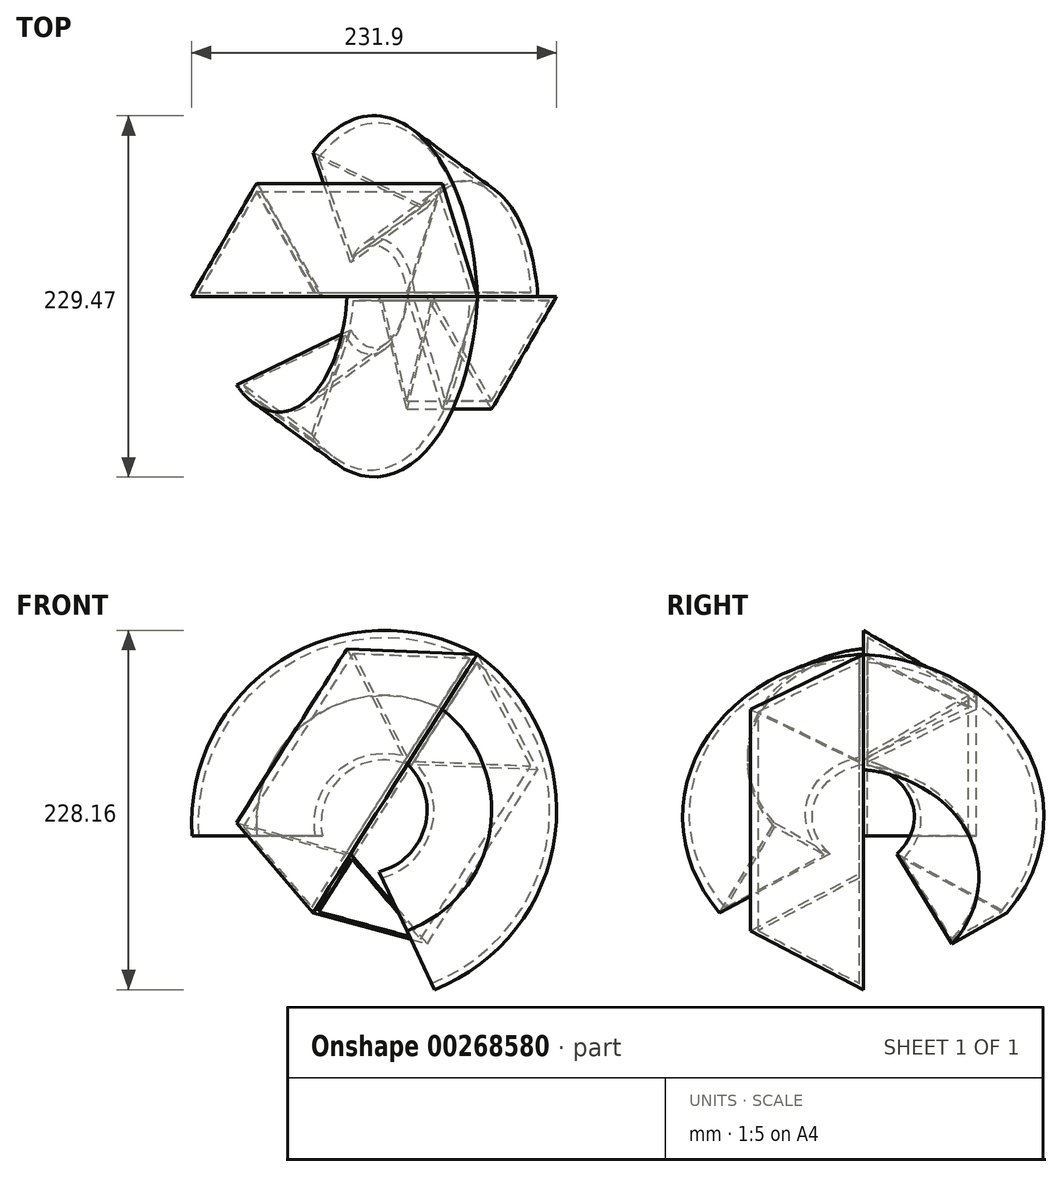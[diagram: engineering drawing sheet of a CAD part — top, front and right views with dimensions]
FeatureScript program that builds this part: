
annotation { "Feature Type Name" : "Feature", "Feature Type Description" : "" }
export const myFeature = defineFeature(function(context is Context, id is Id, definition is map)
    precondition{}
    {
        {
            var Q0;
            Q0=qCreatedBy(makeId("Top.planeOp"),FACE);
            var sketch = newSketch(context, id + "F0", { "sketchPlane" : qUnion([Q0])});
            skCircle(sketch, "E0.cCircle", {"center": v(0, 0) * mm, "radius": 23.91 * mm, "construction": true});
            skLineSegment(sketch, "E0.0", {"start": v(-41.42, -23.91) * mm, "end": v(0, 47.83) * mm});
            skLineSegment(sketch, "E0.1", {"start": v(0, 47.83) * mm, "end": v(41.42, -23.91) * mm});
            skLineSegment(sketch, "E0.2", {"start": v(41.42, -23.91) * mm, "end": v(-41.42, -23.91) * mm});
            skPoint(sketch, "E0.0.midPoint", {"position": v(-20.7, 11.96) * mm});
            skSolve(sketch);
        }
        {
            var Q0;
            Q0=qCreatedBy(makeId("Front.planeOp"),FACE);
            var sketch = newSketch(context, id + "F1", { "sketchPlane" : qUnion([Q0])});
            skArc(sketch, "E1", {"start": v(117.61, 80.29) * mm, "mid": v(35.07, 74.92) * mm, "end": v(0, 0) * mm});
            skSolve(sketch);
        }
        {
            var Q0;
            Q0=makeQuery(id+"F0.imprint","IMPRINT",FACE,{"disambiguationData":[TD([[makeQuery(id+"F0.imprint","IMPRINT",EDGE,{"derivedFrom":sQuery(id+"F0.wireOp",EDGE,"E0.0")}),-1.0]])]});
            var Q1;
            Q1=sQuery(id+"F1.wireOp",EDGE,"E1");
            sweep(context, id + "F2", {"profiles" : qUnion([Q0]), "path" : qUnion([Q1])});
        }
        {
            var Q0;
            Q0=makeQuery(id+"F2.opSweep","SWEPT_BODY",BODY,{"disambiguationData":[OSD([sQuery(id+"F0.wireOp",EDGE,"E0.0"),sQuery(id+"F0.wireOp",EDGE,"E0.1"),sQuery(id+"F0.wireOp",EDGE,"E0.2"),sQuery(id+"F1.wireOp",EDGE,"E1")])]});
            var Q1;
            Q1=makeQuery(id+"F2.opSweep","CAP_EDGE",EDGE,{"disambiguationData":[OSD([sQuery(id+"F0.wireOp",EDGE,"E0.2"),sQuery(id+"F1.wireOp",VERTEX,"E1.start")])],"isStart":false});
            circularPattern(context, id + "F3", {"entities" : qUnion([Q0]), "axis" : qUnion([Q1]), "angle" : 360 * degree, "instanceCount" : 4, "equalSpace" : true});
        }
        {
            var Q0;
            Q0=makeQuery(id+"F3.opPattern","COPY",FACE,{"derivedFrom":makeQuery(id+"F2.opSweep","CAP_FACE",FACE,{"disambiguationData":[OSD([sQuery(id+"F0.wireOp",EDGE,"E0.0"),sQuery(id+"F0.wireOp",EDGE,"E0.1"),sQuery(id+"F0.wireOp",EDGE,"E0.2"),sQuery(id+"F1.wireOp",VERTEX,"E1.end")])],"isStart":true}),"instanceName":"2"});
            var Q1;
            Q1=makeQuery(id+"F3.opPattern","COPY",FACE,{"derivedFrom":makeQuery(id+"F2.opSweep","CAP_FACE",FACE,{"disambiguationData":[OSD([sQuery(id+"F0.wireOp",EDGE,"E0.0"),sQuery(id+"F0.wireOp",EDGE,"E0.1"),sQuery(id+"F0.wireOp",EDGE,"E0.2"),sQuery(id+"F1.wireOp",VERTEX,"E1.end")])],"isStart":true}),"instanceName":"3"});
            var Q2;
            Q2=makeQuery(id+"F2.opSweep","CAP_FACE",FACE,{"disambiguationData":[OSD([sQuery(id+"F0.wireOp",EDGE,"E0.0"),sQuery(id+"F0.wireOp",EDGE,"E0.1"),sQuery(id+"F0.wireOp",EDGE,"E0.2"),sQuery(id+"F1.wireOp",VERTEX,"E1.end")])],"isStart":true});
            var Q3;
            Q3=makeQuery(id+"F3.opPattern","COPY",FACE,{"derivedFrom":makeQuery(id+"F2.opSweep","CAP_FACE",FACE,{"disambiguationData":[OSD([sQuery(id+"F0.wireOp",EDGE,"E0.0"),sQuery(id+"F0.wireOp",EDGE,"E0.1"),sQuery(id+"F0.wireOp",EDGE,"E0.2"),sQuery(id+"F1.wireOp",VERTEX,"E1.end")])],"isStart":true}),"instanceName":"1"});
            shell(context, id + "F4", {"entities" : qUnion([Q0, Q1, Q2, Q3]), "thickness" : 2.54 * mm});
        }
    });
